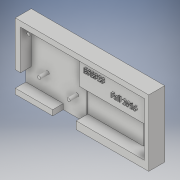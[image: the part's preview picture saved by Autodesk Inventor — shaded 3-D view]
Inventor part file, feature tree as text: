
AUTODESK INVENTOR PART (.ipt)
format: ipt  version: 2017 (Build 210142000, 142)  size: 545,792 bytes
history: native  units: in
note: dims shown in document units (in); Inventor stores cm internally (conversion verified against a paired STEP export)
features: extrude x10, sketch x10
ambient origin geometry x8: Origin, YZ Plane, XZ Plane, XY Plane, X Axis, Y Axis, Z Axis, Center Point
bodies: Solid1 (feature_tree)
feature tree (20):
  extrude  "Extrusion1"  Depth=2.4409in
  extrude  "Extrusion2"  Depth=2.0472in
  extrude  "Extrusion3"  Depth=0.3937in TaperAngle=0.0deg
  extrude  "Extrusion4"  Depth=2.5197in
  extrude  "Extrusion5"  Depth=0.3937in TaperAngle=0.0deg
  extrude  "Extrusion6"  Depth=0.5906in TaperAngle=0.0deg
  extrude  "Extrusion7"  Depth=1.9685in
  extrude  "Extrusion8"  Depth=0.1181in
  extrude  "Extrusion9"  Depth=0.1181in
  extrude  "Extrusion10"  Depth=0.3937in TaperAngle=0.0deg
  sketch  "Sketch3"  dims[d0=4.9213in d1=2.4409in]
  sketch  "Sketch4"  dims[d2=0.5906in d3=0.0in d4=2.0472in]
  sketch  "Sketch5"  dims[d5=2.0472in d7=0.3937in d8=0.0in]
  sketch  "Sketch6"  dims[d9=0.0787in d10=2.5197in]
  sketch  "Sketch7"  dims[d11=1.0433in d12=0.3937in d13=0.0in]
  sketch  "Sketch8"  dims[d14=0.4724in d15=0.5906in d16=0.0in]
  sketch  "Sketch9"  dims[d17=0.4331in d18=0.0in d19=1.9685in]
  sketch  "Sketch10"  dims[d20=1.9685in d28=0.1181in]
  sketch  "Sketch13"  dims[d29=0.1181in d30=0.1181in]
  sketch  "Sketch14"  dims[d31=0.315in d32=0.0in d34=0.3937in d35=0.0in d36=1.4567in d37=0.3937in d38=0.0in d39=0.1181in d40=0.0in d41=0.0591in d42=0.0in]
